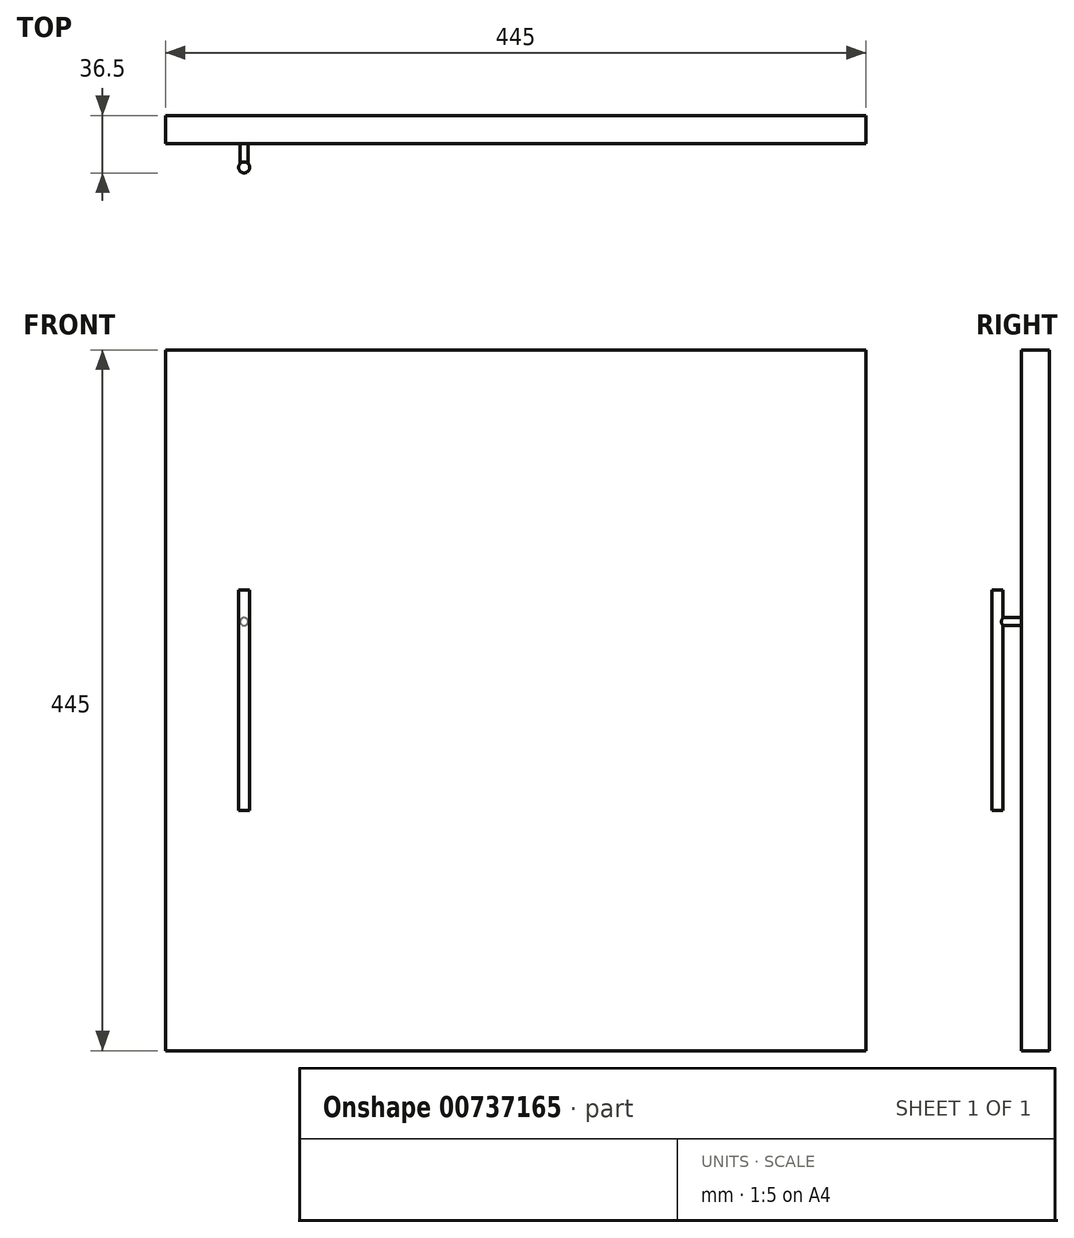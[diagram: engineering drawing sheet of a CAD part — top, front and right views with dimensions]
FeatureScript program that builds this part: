
annotation { "Feature Type Name" : "Feature", "Feature Type Description" : "" }
export const myFeature = defineFeature(function(context is Context, id is Id, definition is map)
    precondition{}
    {
        {
            var Q0;
            Q0=qCreatedBy(makeId("Front.planeOp"),FACE);
            var sketch = newSketch(context, id + "F0", { "sketchPlane" : qUnion([Q0])});
            skLineSegment(sketch, "E0.bottom", {"start": v(222.5, 222.5) * mm, "end": v(-222.5, 222.5) * mm});
            skLineSegment(sketch, "E0.top", {"start": v(222.5, -222.5) * mm, "end": v(-222.5, -222.5) * mm});
            skLineSegment(sketch, "E0.left", {"start": v(222.5, 222.5) * mm, "end": v(222.5, -222.5) * mm});
            skLineSegment(sketch, "E0.right", {"start": v(-222.5, 222.5) * mm, "end": v(-222.5, -222.5) * mm});
            skPoint(sketch, "E0.middle", {"position": v(0, 0) * mm});
            skSolve(sketch);
        }
        {
            var Q0;
            Q0 = qSketchRegion(id + "F0", true);
            extrude(context, id + "F1", {"entities" : qUnion([Q0]), "depth" : 18 * mm, "offsetDistance" : 25 * mm});
        }
        {
            var Q0;
            Q0=makeQuery(id+"F1.opExtrude","CAP_FACE",FACE,{"disambiguationData":[OSD([sQuery(id+"F0.wireOp",EDGE,"E0.bottom"),sQuery(id+"F0.wireOp",EDGE,"E0.top"),sQuery(id+"F0.wireOp",EDGE,"E0.left"),sQuery(id+"F0.wireOp",EDGE,"E0.right")])],"isStart":false});
            var sketch = newSketch(context, id + "F2", { "sketchPlane" : qUnion([Q0])});
            skCircle(sketch, "E1", {"center": v(-172.5, 50) * mm, "radius": 2.5 * mm});
            skSolve(sketch);
        }
        {
            var Q0;
            Q0 = qSketchRegion(id + "F2", true);
            extrude(context, id + "F3", {"entities" : qUnion([Q0]), "operationType" : NewBodyOperationType.ADD, "depth" : 15 * mm, "offsetDistance" : 25 * mm});
        }
        {
            var Q0;
            Q0=qCreatedBy(makeId("Top.planeOp"),FACE);
            var sketch = newSketch(context, id + "F4", { "sketchPlane" : qUnion([Q0])});
            skCircle(sketch, "E2", {"center": v(-172.5, -33) * mm, "radius": 3.5 * mm});
            skSolve(sketch);
        }
        {
            var Q0;
            Q0 = qSketchRegion(id + "F4", true);
            extrude(context, id + "F5", {"entities" : qUnion([Q0]), "operationType" : NewBodyOperationType.ADD, "endBound" : BoundingType.SYMMETRIC, "depth" : 140 * mm, "offsetDistance" : 25 * mm});
        }
    });
